# Revit family: NBS_COBAFlooring_EntMatt_ToughribContract
name_source: partatom
category: Generic Models
revit_build: Autodesk Revit Architecture 2013 (Build: 20130531_2115(x64)
units: mm (PartAtom-declared; Revit-internal decimal feet)

## types (1)
- ToughribContract
    Arrangement = Can be used in recessed matwells or on pedestrian walkways
    AssetType = Fixed
    BIMObjectName = NBS_COBAFlooring_EntranceMatting_ToughribContract
    BaseColour = Black
    BaseMaterial = Latex
    CarpetColourOptions = Blue, Charcoal, Grey, Brown
    Color = Blue, Charcoal, Grey, Brown
    Combustible = No
    Construction = Closed
    Default Elevation = 1200 mm
    Description = Ribbed entrance matting on a roll
    EdgingMaterial = NBS_Concept
    EntranceMattingHeight = 7.5 mm  [stored 0.0246063 ft]
    EntranceMattingMaterial = NBS_COBAFlooring_Carpet_ToughribContract
    EntranceMattingWidth = 2000 mm  [stored 6.56168 ft]
    ExpectedLife = 5 years* If used in the correct environment for the volume and type of traffic expected over the system.
    Finish = Polypropylene ribbed carpet
    HasAntiStaticSurface = No
    HasNonSkidSurface = Yes
    IfcExportAs = IfcCoveringType
    IfcExportType = FLOORING
    IsExternal = No
    ManufacturerName = COBA Flooring
    ManufacturerURL = www.cobaeurope.com/flooring/
    Material = 100% polypropylene pile carpet. Primary (latex) and secondary (gel foam) backing.
    MattingHeight = 7.5 mm (+/- 10%)
    ModelNumber = TRC
    ModelReference = Toughrib Contract
    NBSCertification = www.nationalbimlibrary.com/cert/op1c00jd
    NBSDescription = Entrance matting
    NBSReference = 45-35-35/420
    Name = EntranceMatting_COBAFlooring_ToughribContract
    Pattern = Horizontal ribs
    ProductInformation = www.cobaeurope.com/entrance-matting-systems/toughrib-contract-carpet-matting/
    Size = 2 x 30m roll
    ThermalTransmittance = 0
    TrafficType = Pedestrian, wheel chairs, pushchairs and trolleys
    Uniclass2 = 45-57-11/426
    Version = 1
    WarrantyStartDate = 1900-12-31T23:59:59

note: [stored X ft] marks values corroborated as IEEE doubles in the binary element streams (Revit-internal decimal feet)

## geometry (parser evidence)
native form markers: Sweep x1
no freeform markers — native parametric forms only
